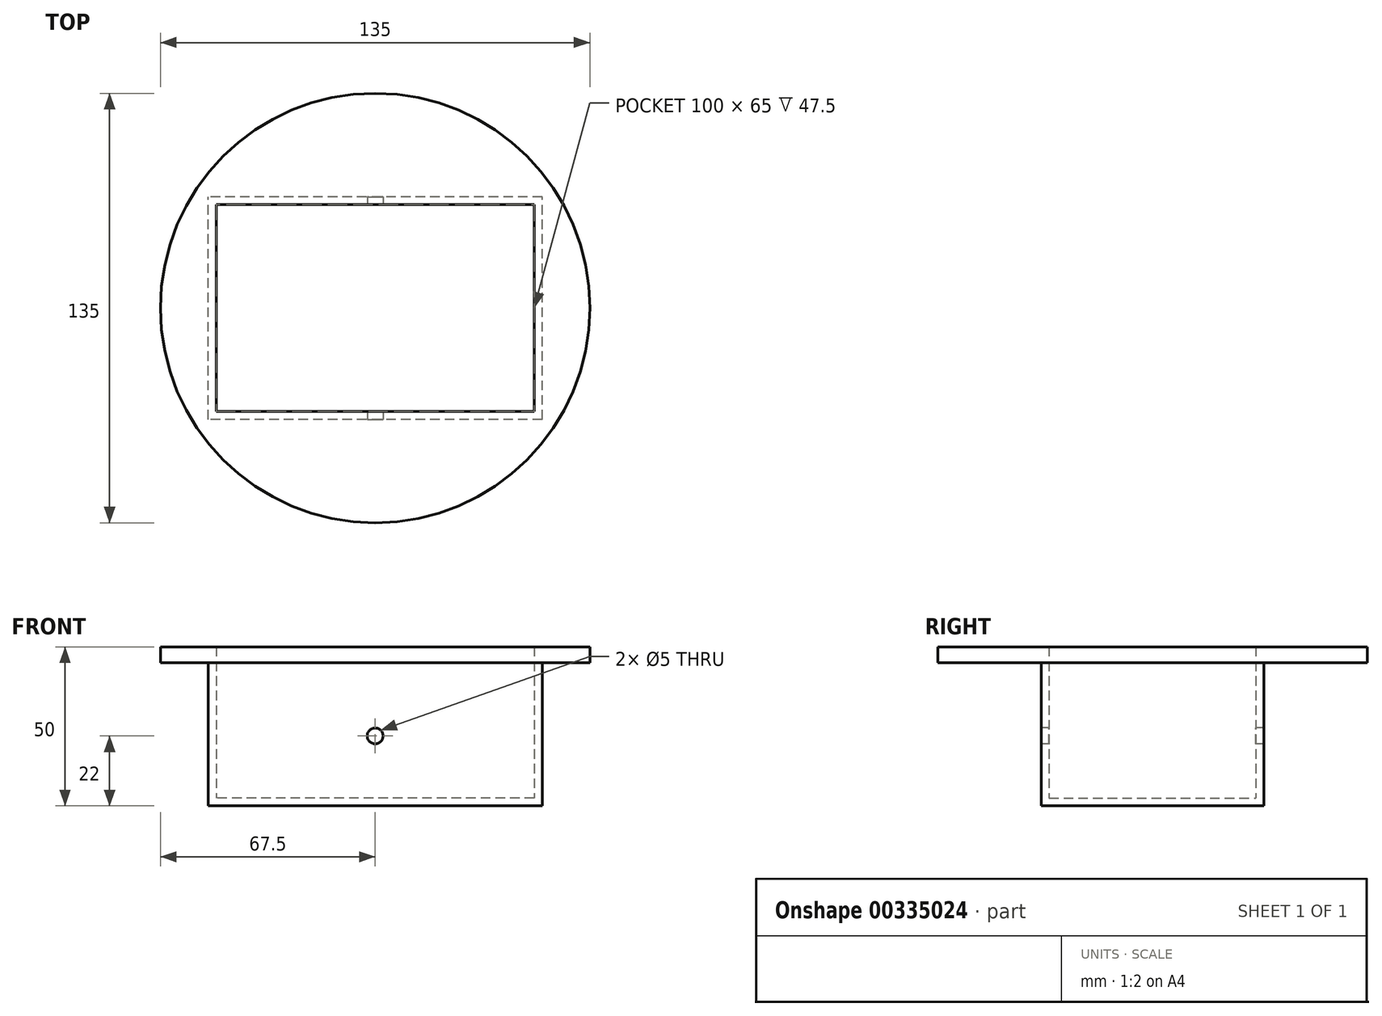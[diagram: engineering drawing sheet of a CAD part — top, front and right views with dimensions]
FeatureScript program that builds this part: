
annotation { "Feature Type Name" : "Feature", "Feature Type Description" : "" }
export const myFeature = defineFeature(function(context is Context, id is Id, definition is map)
    precondition{}
    {
        {
            var Q0;
            Q0=qCreatedBy(makeId("Top.planeOp"),FACE);
            var sketch = newSketch(context, id + "F0", { "sketchPlane" : qUnion([Q0])});
            skLineSegment(sketch, "E0.bottom", {"start": v(52.5, -35) * mm, "end": v(-52.5, -35) * mm});
            skLineSegment(sketch, "E0.top", {"start": v(52.5, 35) * mm, "end": v(-52.5, 35) * mm});
            skLineSegment(sketch, "E0.left", {"start": v(52.5, -35) * mm, "end": v(52.5, 35) * mm});
            skLineSegment(sketch, "E0.right", {"start": v(-52.5, -35) * mm, "end": v(-52.5, 35) * mm});
            skPoint(sketch, "E0.middle", {"position": v(0, 0) * mm});
            skSolve(sketch);
        }
        {
            var Q0;
            Q0=makeQuery(id+"F0.imprint","IMPRINT",FACE,{"disambiguationData":[TD([[makeQuery(id+"F0.imprint","IMPRINT",EDGE,{"derivedFrom":sQuery(id+"F0.wireOp",EDGE,"E0.bottom")}),-1.0]])]});
            extrude(context, id + "F1", {"entities" : qUnion([Q0]), "depth" : 50 * mm});
        }
        {
            var Q0;
            Q0=makeQuery(id+"F1.opExtrude","CAP_FACE",FACE,{"disambiguationData":[OSD([sQuery(id+"F0.wireOp",EDGE,"E0.bottom"),sQuery(id+"F0.wireOp",EDGE,"E0.top"),sQuery(id+"F0.wireOp",EDGE,"E0.left"),sQuery(id+"F0.wireOp",EDGE,"E0.right")])],"isStart":false});
            shell(context, id + "F2", {"entities" : qUnion([Q0]), "thickness" : 2.5 * mm});
        }
        {
            var Q0;
            Q0=makeQuery(id+"F1.opExtrude","CAP_FACE",FACE,{"disambiguationData":[OSD([sQuery(id+"F0.wireOp",EDGE,"E0.bottom"),sQuery(id+"F0.wireOp",EDGE,"E0.top"),sQuery(id+"F0.wireOp",EDGE,"E0.left"),sQuery(id+"F0.wireOp",EDGE,"E0.right")])],"isStart":false});
            var sketch = newSketch(context, id + "F3", { "sketchPlane" : qUnion([Q0])});
            skCircle(sketch, "E1", {"center": v(0, 0) * mm, "radius": 67.5 * mm});
            skSolve(sketch);
        }
        {
            var Q0;
            Q0=makeQuery(id+"F3.imprint","IMPRINT",FACE,{"disambiguationData":[TD([[makeQuery(id+"F3.imprint","IMPRINT",EDGE,{"derivedFrom":sQuery(id+"F3.wireOp",EDGE,"E1")}),1.0]])]});
            extrude(context, id + "F4", {"entities" : qUnion([Q0]), "operationType" : NewBodyOperationType.ADD, "oppositeDirection" : true, "depth" : 5 * mm});
        }
        {
            var Q0;
            Q0=makeQuery(id+"F1.opExtrude","SWEPT_FACE",FACE,{"disambiguationData":[OSD([sQuery(id+"F0.wireOp",EDGE,"E0.bottom")])]});
            var sketch = newSketch(context, id + "F5", { "sketchPlane" : qUnion([Q0])});
            skCircle(sketch, "E2", {"center": v(0, 22) * mm, "radius": 2.5 * mm});
            skSolve(sketch);
        }
        {
            var Q0;
            Q0=makeQuery(id+"F5.imprint","IMPRINT",FACE,{"disambiguationData":[TD([[makeQuery(id+"F5.imprint","IMPRINT",EDGE,{"derivedFrom":sQuery(id+"F5.wireOp",EDGE,"E2")}),1.0]])]});
            extrude(context, id + "F6", {"entities" : qUnion([Q0]), "operationType" : NewBodyOperationType.REMOVE, "endBound" : BoundingType.THROUGH_ALL, "oppositeDirection" : true, "depth" : 25 * mm});
        }
    });
